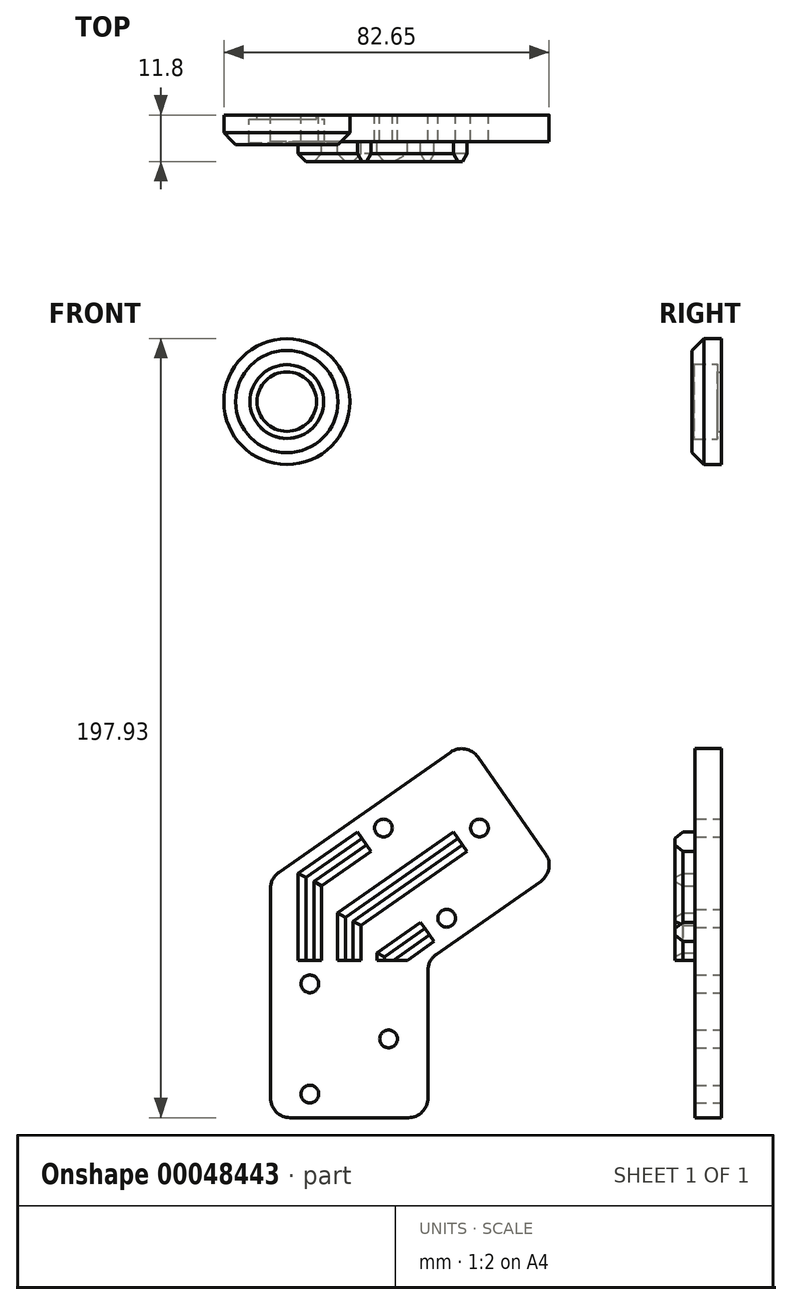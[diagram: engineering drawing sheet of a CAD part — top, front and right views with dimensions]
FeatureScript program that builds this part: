
annotation { "Feature Type Name" : "Feature", "Feature Type Description" : "" }
export const myFeature = defineFeature(function(context is Context, id is Id, definition is map)
    precondition{}
    {
        {
            var Q0;
            Q0=qCreatedBy(makeId("Front.planeOp"),FACE);
            var sketch = newSketch(context, id + "F0", { "sketchPlane" : qUnion([Q0])});
            skLineSegment(sketch, "E0", {"start": v(0, 0) * mm, "end": v(0, -96.03) * mm, "construction": true});
            skLineSegment(sketch, "E1.0", {"start": v(-10, 0) * mm, "end": v(-10, -96.03) * mm, "construction": true});
            skLineSegment(sketch, "E2.0", {"start": v(10, 0) * mm, "end": v(10, -96.03) * mm, "construction": true});
            skLineSegment(sketch, "E3.0", {"start": v(20, 0) * mm, "end": v(20, -96.03) * mm});
            skLineSegment(sketch, "E4.0", {"start": v(-20, 0) * mm, "end": v(-20, -96.03) * mm});
            skLineSegment(sketch, "E5", {"start": v(-20, 0) * mm, "end": v(20, 0) * mm});
            skCircle(sketch, "E6", {"center": v(-15.85, 119.93) * mm, "radius": 100 * mm});
            skCircle(sketch, "E7.0", {"center": v(-15.85, 119.93) * mm, "radius": 120 * mm});
            skCircle(sketch, "E8", {"center": v(-15.85, 119.93) * mm, "radius": 38 * mm});
            skCircle(sketch, "E9", {"center": v(-15.85, 141.93) * mm, "radius": 16 * mm});
            skLineSegment(sketch, "E10", {"start": v(-15.85, 141.93) * mm, "end": v(-31.48, 108.4) * mm});
            skLineSegment(sketch, "E11", {"start": v(-31.48, 108.4) * mm, "end": v(-13.36, 99.94) * mm});
            skLineSegment(sketch, "E12", {"start": v(-31.48, 108.4) * mm, "end": v(-49.6, 116.85) * mm});
            skLineSegment(sketch, "E13", {"start": v(-63.83, 137.16) * mm, "end": v(6.54, 36.66) * mm});
            skLineSegment(sketch, "E14.0", {"start": v(-46.44, 147.2) * mm, "end": v(23.93, 46.7) * mm});
            skLineSegment(sketch, "E15.0", {"start": v(-86.14, 151.59) * mm, "end": v(20, 0) * mm});
            skLineSegment(sketch, "E16.0", {"start": v(-37.86, 152.37) * mm, "end": v(52.77, 22.94) * mm});
            skLineSegment(sketch, "E17", {"start": v(20, 0) * mm, "end": v(52.77, 22.94) * mm});
            skSolve(sketch);
        }
        {
            var Q0;
            Q0=qCreatedBy(makeId("Front.planeOp"),FACE);
            var sketch = newSketch(context, id + "F1", { "sketchPlane" : qUnion([Q0])});
            skLineSegment(sketch, "E18", {"start": v(-20, -40) * mm, "end": v(20, -40) * mm});
            skLineSegment(sketch, "E19", {"start": v(20, -40) * mm, "end": v(20, 0) * mm});
            skLineSegment(sketch, "E20", {"start": v(-20, 20.82) * mm, "end": v(-20, -40) * mm});
            skLineSegment(sketch, "E21", {"start": v(20, 0) * mm, "end": v(52.77, 22.94) * mm});
            skLineSegment(sketch, "E22", {"start": v(52.77, 22.94) * mm, "end": v(29.82, 55.7) * mm});
            skLineSegment(sketch, "E23", {"start": v(29.82, 55.7) * mm, "end": v(-20, 20.82) * mm});
            skPoint(sketch, "E24", {"position": v(-10, -34) * mm});
            skPoint(sketch, "E25", {"position": v(-10, -6) * mm});
            skPoint(sketch, "E26", {"position": v(10, -20) * mm});
            skPoint(sketch, "E27", {"position": v(8.69, 33.59) * mm});
            skPoint(sketch, "E28", {"position": v(24.75, 10.65) * mm});
            skPoint(sketch, "E29", {"position": v(33.1, 33.6) * mm});
            skLineSegment(sketch, "E30", {"start": v(10, -20) * mm, "end": v(-3.86, -20) * mm, "construction": true});
            skLineSegment(sketch, "E31", {"start": v(33.1, 33.6) * mm, "end": v(15.29, 21.12) * mm, "construction": true});
            skLineSegment(sketch, "E32", {"start": v(41.3, 39.33) * mm, "end": v(33.1, 33.6) * mm, "construction": true});
            skLineSegment(sketch, "E33", {"start": v(10, -20) * mm, "end": v(20, -20) * mm, "construction": true});
            skSolve(sketch);
        }
        {
            var Q0;
            Q0=makeQuery(id+"F1.imprint","IMPRINT",FACE,{"disambiguationData":[TD([[makeQuery(id+"F1.imprint","IMPRINT",EDGE,{"derivedFrom":sQuery(id+"F1.wireOp",EDGE,"E18")}),1.0]])]});
            var Q1;
            Q1=sQuery(id+"F1.wireOp",EDGE,"E19");
            extrude(context, id + "F2", {"entities" : qUnion([Q0]), "surfaceEntities" : qUnion([Q1]), "depth" : 6.8 * mm});
        }
        {
            var Q0;
            Q0=sQuery(id+"F1.wireOp",VERTEX,"E25");
            var Q1;
            Q1=sQuery(id+"F1.wireOp",VERTEX,"E26");
            var Q2;
            Q2=sQuery(id+"F1.wireOp",VERTEX,"E24");
            var Q3;
            Q3=sQuery(id+"F1.wireOp",VERTEX,"E27");
            var Q4;
            Q4=sQuery(id+"F1.wireOp",VERTEX,"E28");
            var Q5;
            Q5=sQuery(id+"F1.wireOp",VERTEX,"E29");
            var Q6;
            Q6=makeQuery(id+"F2.opExtrude","SWEPT_BODY",BODY,{"disambiguationData":[OSD([sQuery(id+"F1.wireOp",EDGE,"E18"),sQuery(id+"F1.wireOp",EDGE,"E19"),sQuery(id+"F1.wireOp",EDGE,"E20"),sQuery(id+"F1.wireOp",EDGE,"E21"),sQuery(id+"F1.wireOp",EDGE,"E22"),sQuery(id+"F1.wireOp",EDGE,"E23")])]});
            hole(context, id + "F3", {"style" : HoleStyle.SIMPLE, "holeDiameter" : 4.5 * mm, "endStyle" : HoleEndStyle.THROUGH, "oppositeDirection" : true, "locations" : qUnion([Q0, Q1, Q2, Q3, Q4, Q5]), "scope" : qUnion([Q6])});
        }
        {
            var Q0;
            Q0=makeQuery(id+"F2.opExtrude","CAP_FACE",FACE,{"disambiguationData":[OSD([sQuery(id+"F1.wireOp",EDGE,"E18"),sQuery(id+"F1.wireOp",EDGE,"E19"),sQuery(id+"F1.wireOp",EDGE,"E20"),sQuery(id+"F1.wireOp",EDGE,"E21"),sQuery(id+"F1.wireOp",EDGE,"E22"),sQuery(id+"F1.wireOp",EDGE,"E23")])],"isStart":false});
            var sketch = newSketch(context, id + "F4", { "sketchPlane" : qUnion([Q0])});
            skLineSegment(sketch, "E34", {"start": v(28.19, 30.15) * mm, "end": v(0, 10.41) * mm});
            skLineSegment(sketch, "E35", {"start": v(0, 10.41) * mm, "end": v(0, 0) * mm});
            skLineSegment(sketch, "E36", {"start": v(19.84, 7.2) * mm, "end": v(10, 0.32) * mm});
            skLineSegment(sketch, "E37", {"start": v(10, 0.32) * mm, "end": v(10, 0) * mm});
            skLineSegment(sketch, "E38", {"start": v(3.78, 30.15) * mm, "end": v(-10, 20.5) * mm});
            skLineSegment(sketch, "E39", {"start": v(-10, 20.5) * mm, "end": v(-10, 0) * mm});
            skLineSegment(sketch, "E40.0", {"start": v(-13, 22.06) * mm, "end": v(-13, 0) * mm});
            skLineSegment(sketch, "E40.1", {"start": v(2.05, 32.6) * mm, "end": v(-13, 22.06) * mm});
            skLineSegment(sketch, "E41.0", {"start": v(-7, 18.94) * mm, "end": v(-7, 0) * mm});
            skLineSegment(sketch, "E41.1", {"start": v(5.5, 27.69) * mm, "end": v(-7, 18.94) * mm});
            skLineSegment(sketch, "E42.0", {"start": v(-3, 11.97) * mm, "end": v(-3, 0) * mm});
            skLineSegment(sketch, "E42.1", {"start": v(26.47, 32.6) * mm, "end": v(-3, 11.97) * mm});
            skLineSegment(sketch, "E43.0", {"start": v(3, 8.85) * mm, "end": v(3, 0) * mm});
            skLineSegment(sketch, "E43.1", {"start": v(29.9, 27.7) * mm, "end": v(3, 8.85) * mm});
            skLineSegment(sketch, "E44.0", {"start": v(7, 1.88) * mm, "end": v(7, 0) * mm});
            skLineSegment(sketch, "E44.1", {"start": v(18.11, 9.67) * mm, "end": v(7, 1.88) * mm});
            skLineSegment(sketch, "E45.0", {"start": v(21.56, 4.75) * mm, "end": v(14.77, 0) * mm});
            skLineSegment(sketch, "E46", {"start": v(2.05, 32.6) * mm, "end": v(5.5, 27.69) * mm});
            skLineSegment(sketch, "E47", {"start": v(26.47, 32.6) * mm, "end": v(29.9, 27.7) * mm});
            skLineSegment(sketch, "E48", {"start": v(18.11, 9.67) * mm, "end": v(21.56, 4.75) * mm});
            skLineSegment(sketch, "E49", {"start": v(-13, 0) * mm, "end": v(-7, 0) * mm});
            skLineSegment(sketch, "E50", {"start": v(-3, 0) * mm, "end": v(3, 0) * mm});
            skLineSegment(sketch, "E51", {"start": v(7, 0) * mm, "end": v(14.77, 0) * mm});
            skSolve(sketch);
        }
        {
            var Q0;
            Q0 = qSketchRegion(id + "F4", true);
            extrude(context, id + "F5", {"entities" : qUnion([Q0]), "operationType" : NewBodyOperationType.ADD, "depth" : 5 * mm});
        }
        {
            var Q0;
            Q0=makeQuery(id+"F5.opExtrude","CAP_EDGE",EDGE,{"disambiguationData":[OSD([sQuery(id+"F4.wireOp",EDGE,"E40.1")])],"isStart":false});
            var Q1;
            Q1=makeQuery(id+"F5.opExtrude","CAP_EDGE",EDGE,{"disambiguationData":[OSD([sQuery(id+"F4.wireOp",EDGE,"E40.0")])],"isStart":false});
            var Q2;
            Q2=makeQuery(id+"F5.opExtrude","CAP_EDGE",EDGE,{"disambiguationData":[OSD([sQuery(id+"F4.wireOp",EDGE,"E41.1")])],"isStart":false});
            var Q3;
            Q3=makeQuery(id+"F5.opExtrude","CAP_EDGE",EDGE,{"disambiguationData":[OSD([sQuery(id+"F4.wireOp",EDGE,"E41.0")])],"isStart":false});
            var Q4;
            Q4=makeQuery(id+"F5.opExtrude","CAP_EDGE",EDGE,{"disambiguationData":[OSD([sQuery(id+"F4.wireOp",EDGE,"E42.1")])],"isStart":false});
            var Q5;
            Q5=makeQuery(id+"F5.opExtrude","CAP_EDGE",EDGE,{"disambiguationData":[OSD([sQuery(id+"F4.wireOp",EDGE,"E42.0")])],"isStart":false});
            var Q6;
            Q6=makeQuery(id+"F5.opExtrude","CAP_EDGE",EDGE,{"disambiguationData":[OSD([sQuery(id+"F4.wireOp",EDGE,"E43.1")])],"isStart":false});
            var Q7;
            Q7=makeQuery(id+"F5.opExtrude","CAP_EDGE",EDGE,{"disambiguationData":[OSD([sQuery(id+"F4.wireOp",EDGE,"E43.0")])],"isStart":false});
            var Q8;
            Q8=makeQuery(id+"F5.opExtrude","CAP_EDGE",EDGE,{"disambiguationData":[OSD([sQuery(id+"F4.wireOp",EDGE,"E44.1")])],"isStart":false});
            var Q9;
            Q9=makeQuery(id+"F5.opExtrude","CAP_EDGE",EDGE,{"disambiguationData":[OSD([sQuery(id+"F4.wireOp",EDGE,"E45.0")])],"isStart":false});
            var Q10;
            Q10=makeQuery(id+"F5.opExtrude","CAP_EDGE",EDGE,{"disambiguationData":[OSD([sQuery(id+"F4.wireOp",EDGE,"E44.0")])],"isStart":false});
            chamfer(context, id + "F6", {"entities" : qUnion([Q0, Q1, Q2, Q3, Q4, Q5, Q6, Q7, Q8, Q9, Q10]), "width" : 2 * mm, "tangentPropagation" : true});
        }
        {
            var Q0;
            Q0=makeQuery(id+"F2.opExtrude","SWEPT_EDGE",EDGE,{"disambiguationData":[OSD([sQuery(id+"F1.wireOp",EDGE,"E20"),sQuery(id+"F1.wireOp",EDGE,"E23")])]});
            var Q1;
            Q1=makeQuery(id+"F2.opExtrude","SWEPT_EDGE",EDGE,{"disambiguationData":[OSD([sQuery(id+"F1.wireOp",EDGE,"E22"),sQuery(id+"F1.wireOp",EDGE,"E23")])]});
            var Q2;
            Q2=makeQuery(id+"F2.opExtrude","SWEPT_EDGE",EDGE,{"disambiguationData":[OSD([sQuery(id+"F1.wireOp",EDGE,"E18"),sQuery(id+"F1.wireOp",EDGE,"E20")])]});
            var Q3;
            Q3=makeQuery(id+"F2.opExtrude","SWEPT_EDGE",EDGE,{"disambiguationData":[OSD([sQuery(id+"F1.wireOp",EDGE,"E18"),sQuery(id+"F1.wireOp",EDGE,"E19")])]});
            var Q4;
            Q4=makeQuery(id+"F2.opExtrude","SWEPT_EDGE",EDGE,{"disambiguationData":[OSD([sQuery(id+"F1.wireOp",EDGE,"E19"),sQuery(id+"F1.wireOp",EDGE,"E21")])]});
            var Q5;
            Q5=makeQuery(id+"F2.opExtrude","SWEPT_EDGE",EDGE,{"disambiguationData":[OSD([sQuery(id+"F1.wireOp",EDGE,"E21"),sQuery(id+"F1.wireOp",EDGE,"E22")])]});
            fillet(context, id + "F7", {"entities" : qUnion([Q0, Q1, Q2, Q3, Q4, Q5]), "radius" : 5 * mm, "tangentPropagation" : true, "allowEdgeOverflow" : false});
        }
        {
            var Q0;
            Q0=sQuery(id+"F0.wireOp",VERTEX,"E10.start");
            var Q1;
            Q1=qCreatedBy(makeId("Top.planeOp"),FACE);
            cPlane(context, id + "F8", {"entities" : qUnion([Q0, Q1]), "cplaneType" : CPlaneType.PLANE_POINT, "offset" : 150 * mm, "width" : 150 * mm, "height" : 150 * mm});
        }
        {
            var Q0;
            Q0=qCreatedBy(id+"F8.planeOp",FACE);
            var sketch = newSketch(context, id + "F9", { "sketchPlane" : qUnion([Q0])});
            skLineSegment(sketch, "E52", {"start": v(-15.85, 0) * mm, "end": v(-15.85, -79.96) * mm});
            skLineSegment(sketch, "E53", {"start": v(-25.2, -7) * mm, "end": v(-25.2, -7.5) * mm});
            skLineSegment(sketch, "E54", {"start": v(-25.2, -7.5) * mm, "end": v(-31.85, -7.5) * mm});
            skLineSegment(sketch, "E55", {"start": v(-31.85, -7.5) * mm, "end": v(-31.85, 0) * mm});
            skLineSegment(sketch, "E56", {"start": v(-31.85, 0) * mm, "end": v(-23.4, 0) * mm});
            skLineSegment(sketch, "E57", {"start": v(-23.4, 0) * mm, "end": v(-23.4, -1) * mm});
            skLineSegment(sketch, "E58", {"start": v(-25.2, -7) * mm, "end": v(-25.4, -7) * mm});
            skLineSegment(sketch, "E59", {"start": v(-25.4, -7) * mm, "end": v(-25.4, -1) * mm});
            skLineSegment(sketch, "E60", {"start": v(-25.4, -1) * mm, "end": v(-23.4, -1) * mm});
            skSolve(sketch);
        }
        {
            var Q0;
            Q0=makeQuery(id+"F9.imprint","IMPRINT",FACE,{"disambiguationData":[TD([[makeQuery(id+"F9.imprint","IMPRINT",EDGE,{"derivedFrom":sQuery(id+"F9.wireOp",EDGE,"E53")}),-1.0]])]});
            var Q1;
            Q1=sQuery(id+"F9.wireOp",EDGE,"E52");
            revolve(context, id + "F10", {"entities" : qUnion([Q0]), "axis" : qUnion([Q1]), "revolveType" : RevolveType.FULL});
        }
        {
            var Q0;
            Q0=makeQuery(id+"F10.opRevolve","SWEPT_EDGE",EDGE,{"disambiguationData":[OSD([sQuery(id+"F9.wireOp",EDGE,"E54"),sQuery(id+"F9.wireOp",EDGE,"E55")])]});
            chamfer(context, id + "F11", {"entities" : qUnion([Q0]), "width" : 3 * mm, "tangentPropagation" : true});
        }
    });
